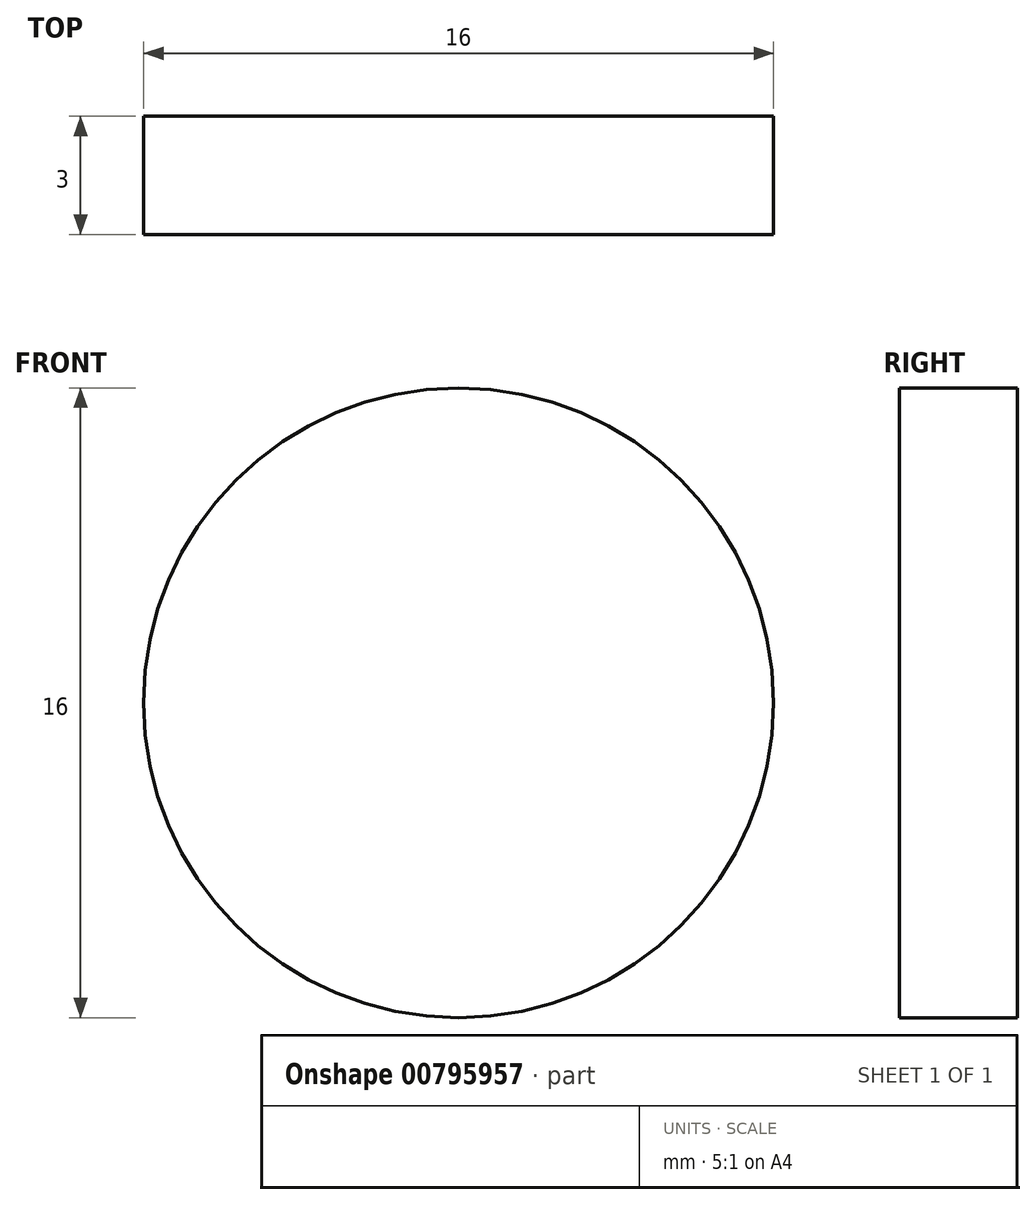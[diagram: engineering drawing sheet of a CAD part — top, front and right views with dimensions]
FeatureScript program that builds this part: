
annotation { "Feature Type Name" : "Feature", "Feature Type Description" : "" }
export const myFeature = defineFeature(function(context is Context, id is Id, definition is map)
    precondition{}
    {
        {
            var Q0;
            Q0=qCreatedBy(makeId("Front.planeOp"),FACE);
            var sketch = newSketch(context, id + "F0", { "sketchPlane" : qUnion([Q0])});
            skLineSegment(sketch, "E0.bottom", {"start": v(72.5, 15) * mm, "end": v(-72.5, 15) * mm});
            skLineSegment(sketch, "E0.top", {"start": v(72.5, -15) * mm, "end": v(-72.5, -15) * mm});
            skLineSegment(sketch, "E0.left", {"start": v(72.5, 15) * mm, "end": v(72.5, -15) * mm});
            skLineSegment(sketch, "E0.right", {"start": v(-72.5, 15) * mm, "end": v(-72.5, -15) * mm});
            skPoint(sketch, "E0.middle", {"position": v(0, 0) * mm});
            skSolve(sketch);
        }
        {
            var Q0;
            Q0=makeQuery(id+"F0.imprint","IMPRINT",FACE,{"disambiguationData":[TD([[makeQuery(id+"F0.imprint","IMPRINT",EDGE,{"derivedFrom":sQuery(id+"F0.wireOp",EDGE,"E0.bottom")}),1.0]])]});
            extrude(context, id + "F1", {"entities" : qUnion([Q0]), "depth" : 3 * mm, "offsetDistance" : 25 * mm});
        }
        {
            var Q0;
            Q0=makeQuery(id+"F1.opExtrude","CAP_FACE",FACE,{"disambiguationData":[OSD([sQuery(id+"F0.wireOp",EDGE,"E0.bottom"),sQuery(id+"F0.wireOp",EDGE,"E0.top"),sQuery(id+"F0.wireOp",EDGE,"E0.left"),sQuery(id+"F0.wireOp",EDGE,"E0.right")])],"isStart":false});
            var sketch = newSketch(context, id + "F2", { "sketchPlane" : qUnion([Q0])});
            skLineSegment(sketch, "E1", {"start": v(-75, -15) * mm, "end": v(-72.5, -15) * mm, "construction": true});
            skLineSegment(sketch, "E2.bottom", {"start": v(-75, -15) * mm, "end": v(-65, -15) * mm});
            skLineSegment(sketch, "E2.top", {"start": v(-75, -12) * mm, "end": v(-65, -12) * mm});
            skLineSegment(sketch, "E2.left", {"start": v(-75, -15) * mm, "end": v(-75, -12) * mm});
            skLineSegment(sketch, "E2.right", {"start": v(-65, -15) * mm, "end": v(-65, -12) * mm});
            skLineSegment(sketch, "E3.0.1.0", {"start": v(-75, 15) * mm, "end": v(-65, 15) * mm});
            skLineSegment(sketch, "E3.0.1.1", {"start": v(-75, 12) * mm, "end": v(-65, 12) * mm});
            skLineSegment(sketch, "E3.0.1.2", {"start": v(-65, 12) * mm, "end": v(-65, 15) * mm});
            skLineSegment(sketch, "E3.0.1.3", {"start": v(-75, 12) * mm, "end": v(-75, 15) * mm});
            skLineSegment(sketch, "E3.1.0.0", {"start": v(-55, -12) * mm, "end": v(-45, -12) * mm});
            skLineSegment(sketch, "E3.1.0.1", {"start": v(-55, -15) * mm, "end": v(-45, -15) * mm});
            skLineSegment(sketch, "E3.1.0.2", {"start": v(-45, -15) * mm, "end": v(-45, -12) * mm});
            skLineSegment(sketch, "E3.1.0.3", {"start": v(-55, -15) * mm, "end": v(-55, -12) * mm});
            skLineSegment(sketch, "E3.1.1.0", {"start": v(-55, 15) * mm, "end": v(-45, 15) * mm});
            skLineSegment(sketch, "E3.1.1.1", {"start": v(-55, 12) * mm, "end": v(-45, 12) * mm});
            skLineSegment(sketch, "E3.1.1.2", {"start": v(-45, 12) * mm, "end": v(-45, 15) * mm});
            skLineSegment(sketch, "E3.1.1.3", {"start": v(-55, 12) * mm, "end": v(-55, 15) * mm});
            skLineSegment(sketch, "E3.2.0.0", {"start": v(-35, -12) * mm, "end": v(-25, -12) * mm});
            skLineSegment(sketch, "E3.2.0.1", {"start": v(-35, -15) * mm, "end": v(-25, -15) * mm});
            skLineSegment(sketch, "E3.2.0.2", {"start": v(-25, -15) * mm, "end": v(-25, -12) * mm});
            skLineSegment(sketch, "E3.2.0.3", {"start": v(-35, -15) * mm, "end": v(-35, -12) * mm});
            skLineSegment(sketch, "E3.2.1.0", {"start": v(-35, 15) * mm, "end": v(-25, 15) * mm});
            skLineSegment(sketch, "E3.2.1.1", {"start": v(-35, 12) * mm, "end": v(-25, 12) * mm});
            skLineSegment(sketch, "E3.2.1.2", {"start": v(-25, 12) * mm, "end": v(-25, 15) * mm});
            skLineSegment(sketch, "E3.2.1.3", {"start": v(-35, 12) * mm, "end": v(-35, 15) * mm});
            skLineSegment(sketch, "E3.3.0.0", {"start": v(-15, -12) * mm, "end": v(-5, -12) * mm});
            skLineSegment(sketch, "E3.3.0.1", {"start": v(-15, -15) * mm, "end": v(-5, -15) * mm});
            skLineSegment(sketch, "E3.3.0.2", {"start": v(-5, -15) * mm, "end": v(-5, -12) * mm});
            skLineSegment(sketch, "E3.3.0.3", {"start": v(-15, -15) * mm, "end": v(-15, -12) * mm});
            skLineSegment(sketch, "E3.3.1.0", {"start": v(-15, 15) * mm, "end": v(-5, 15) * mm});
            skLineSegment(sketch, "E3.3.1.1", {"start": v(-15, 12) * mm, "end": v(-5, 12) * mm});
            skLineSegment(sketch, "E3.3.1.2", {"start": v(-5, 12) * mm, "end": v(-5, 15) * mm});
            skLineSegment(sketch, "E3.3.1.3", {"start": v(-15, 12) * mm, "end": v(-15, 15) * mm});
            skLineSegment(sketch, "E3.4.0.0", {"start": v(5, -12) * mm, "end": v(15, -12) * mm});
            skLineSegment(sketch, "E3.4.0.1", {"start": v(5, -15) * mm, "end": v(15, -15) * mm});
            skLineSegment(sketch, "E3.4.0.2", {"start": v(15, -15) * mm, "end": v(15, -12) * mm});
            skLineSegment(sketch, "E3.4.0.3", {"start": v(5, -15) * mm, "end": v(5, -12) * mm});
            skLineSegment(sketch, "E3.4.1.0", {"start": v(5, 15) * mm, "end": v(15, 15) * mm});
            skLineSegment(sketch, "E3.4.1.1", {"start": v(5, 12) * mm, "end": v(15, 12) * mm});
            skLineSegment(sketch, "E3.4.1.2", {"start": v(15, 12) * mm, "end": v(15, 15) * mm});
            skLineSegment(sketch, "E3.4.1.3", {"start": v(5, 12) * mm, "end": v(5, 15) * mm});
            skLineSegment(sketch, "E3.5.0.0", {"start": v(25, -12) * mm, "end": v(35, -12) * mm});
            skLineSegment(sketch, "E3.5.0.1", {"start": v(25, -15) * mm, "end": v(35, -15) * mm});
            skLineSegment(sketch, "E3.5.0.2", {"start": v(35, -15) * mm, "end": v(35, -12) * mm});
            skLineSegment(sketch, "E3.5.0.3", {"start": v(25, -15) * mm, "end": v(25, -12) * mm});
            skLineSegment(sketch, "E3.5.1.0", {"start": v(25, 15) * mm, "end": v(35, 15) * mm});
            skLineSegment(sketch, "E3.5.1.1", {"start": v(25, 12) * mm, "end": v(35, 12) * mm});
            skLineSegment(sketch, "E3.5.1.2", {"start": v(35, 12) * mm, "end": v(35, 15) * mm});
            skLineSegment(sketch, "E3.5.1.3", {"start": v(25, 12) * mm, "end": v(25, 15) * mm});
            skLineSegment(sketch, "E3.6.0.0", {"start": v(45, -12) * mm, "end": v(55, -12) * mm});
            skLineSegment(sketch, "E3.6.0.1", {"start": v(45, -15) * mm, "end": v(55, -15) * mm});
            skLineSegment(sketch, "E3.6.0.2", {"start": v(55, -15) * mm, "end": v(55, -12) * mm});
            skLineSegment(sketch, "E3.6.0.3", {"start": v(45, -15) * mm, "end": v(45, -12) * mm});
            skLineSegment(sketch, "E3.6.1.0", {"start": v(45, 15) * mm, "end": v(55, 15) * mm});
            skLineSegment(sketch, "E3.6.1.1", {"start": v(45, 12) * mm, "end": v(55, 12) * mm});
            skLineSegment(sketch, "E3.6.1.2", {"start": v(55, 12) * mm, "end": v(55, 15) * mm});
            skLineSegment(sketch, "E3.6.1.3", {"start": v(45, 12) * mm, "end": v(45, 15) * mm});
            skLineSegment(sketch, "E3.direction1", {"start": v(-75, -12) * mm, "end": v(-55, -12) * mm, "construction": true});
            skLineSegment(sketch, "E3.direction2", {"start": v(-75, -12) * mm, "end": v(-75, 15) * mm, "construction": true});
            skLineSegment(sketch, "E4.0.7.0", {"start": v(65, -12) * mm, "end": v(75, -12) * mm});
            skLineSegment(sketch, "E4.3.7.0", {"start": v(65, -15) * mm, "end": v(75, -15) * mm});
            skLineSegment(sketch, "E4.6.7.0", {"start": v(75, -15) * mm, "end": v(75, -12) * mm});
            skLineSegment(sketch, "E4.9.7.0", {"start": v(65, -15) * mm, "end": v(65, -12) * mm});
            skLineSegment(sketch, "E4.0.7.1", {"start": v(65, 15) * mm, "end": v(75, 15) * mm});
            skLineSegment(sketch, "E4.3.7.1", {"start": v(65, 12) * mm, "end": v(75, 12) * mm});
            skLineSegment(sketch, "E4.6.7.1", {"start": v(75, 12) * mm, "end": v(75, 15) * mm});
            skLineSegment(sketch, "E4.9.7.1", {"start": v(65, 12) * mm, "end": v(65, 15) * mm});
            skSolve(sketch);
        }
        {
            var Q0;
            Q0=qSketchRegion(id+"F2",true);
            extrude(context, id + "F3", {"entities" : qUnion([Q0]), "operationType" : NewBodyOperationType.REMOVE, "oppositeDirection" : true, "depth" : 25 * mm, "offsetDistance" : 25 * mm});
        }
        {
            var Q0;
            Q0=makeQuery(id+"F1.opExtrude","SWEPT_FACE",FACE,{"disambiguationData":[OSD([sQuery(id+"F0.wireOp",EDGE,"E0.left")])]});
            var Q1;
            Q1=makeQuery(id+"F1.opExtrude","SWEPT_FACE",FACE,{"disambiguationData":[OSD([sQuery(id+"F0.wireOp",EDGE,"E0.right")])]});
            extrude(context, id + "F4", {"entities" : qUnion([Q0, Q1]), "operationType" : NewBodyOperationType.ADD, "depth" : 5 * mm, "offsetDistance" : 25 * mm});
        }
        {
            var Q0;
            Q0=makeQuery(id+"F1.opExtrude","SWEPT_FACE",FACE,{"disambiguationData":[OSD([sQuery(id+"F0.wireOp",EDGE,"E0.right")])]});
            extrude(context, id + "F5", {"entities" : qUnion([Q0]), "operationType" : NewBodyOperationType.ADD, "depth" : 5 * mm, "offsetDistance" : 25 * mm});
        }
        {
            var Q0;
            {var subQ0=sQuery(id+"F0.wireOp",EDGE,"E0.right");var subQ1=sQuery(id+"F0.wireOp",EDGE,"E0.left");Q0=makeQuery(id+"F5.boolean.opBoolean","MERGE",FACE,{"derivedFrom":[makeQuery(id+"F4.boolean.opBoolean","MERGE",FACE,{"derivedFrom":[makeQuery(id+"F1.opExtrude","CAP_FACE",FACE,{"disambiguationData":[OSD([sQuery(id+"F0.wireOp",EDGE,"E0.bottom"),sQuery(id+"F0.wireOp",EDGE,"E0.top"),subQ1,subQ0])],"isStart":true}),makeQuery(id+"F4.opExtrude","SWEPT_FACE",FACE,{"disambiguationData":[OSD([subQ1]),TDD([makeQuery(id+"F1.opExtrude","CAP_EDGE",EDGE,{"disambiguationData":[OSD([subQ1])],"isStart":true})])]})]}),makeQuery(id+"F5.opExtrude","SWEPT_FACE",FACE,{"disambiguationData":[OSD([subQ0]),TDD([makeQuery(id+"F1.opExtrude","CAP_EDGE",EDGE,{"disambiguationData":[OSD([subQ0])],"isStart":true})])]})]});}
            var sketch = newSketch(context, id + "F6", { "sketchPlane" : qUnion([Q0])});
            skLineSegment(sketch, "E5.bottom", {"start": v(75.5, -12) * mm, "end": v(72.5, -12) * mm});
            skLineSegment(sketch, "E5.top", {"start": v(75.5, 0) * mm, "end": v(72.5, 0) * mm});
            skLineSegment(sketch, "E5.left", {"start": v(75.5, -12) * mm, "end": v(75.5, 0) * mm});
            skLineSegment(sketch, "E5.right", {"start": v(72.5, -12) * mm, "end": v(72.5, 0) * mm});
            skLineSegment(sketch, "E6", {"start": v(0, 15) * mm, "end": v(0, -24.82) * mm, "construction": true});
            skLineSegment(sketch, "E7.MirrorCS", {"start": v(-75.5, -12) * mm, "end": v(-75.5, 0) * mm});
            skLineSegment(sketch, "E8.MirrorCS", {"start": v(-75.5, 0) * mm, "end": v(-72.5, 0) * mm});
            skLineSegment(sketch, "E9.MirrorCS", {"start": v(-75.5, -12) * mm, "end": v(-72.5, -12) * mm});
            skLineSegment(sketch, "E10.MirrorCS", {"start": v(-72.5, -12) * mm, "end": v(-72.5, 0) * mm});
            skSolve(sketch);
        }
        {
            var Q0;
            Q0=makeQuery(id+"F6.imprint","IMPRINT",FACE,{"disambiguationData":[TD([[makeQuery(id+"F6.imprint","IMPRINT",EDGE,{"derivedFrom":sQuery(id+"F6.wireOp",EDGE,"E7.MirrorCS")}),-1.0]])]});
            var Q1;
            Q1=makeQuery(id+"F6.imprint","IMPRINT",FACE,{"disambiguationData":[TD([[makeQuery(id+"F6.imprint","IMPRINT",EDGE,{"derivedFrom":sQuery(id+"F6.wireOp",EDGE,"E5.bottom")}),-1.0]])]});
            extrude(context, id + "F7", {"entities" : qUnion([Q0, Q1]), "operationType" : NewBodyOperationType.REMOVE, "oppositeDirection" : true, "depth" : 25 * mm, "offsetDistance" : 25 * mm});
        }
        {
            var Q0;
            {var subQ0=sQuery(id+"F0.wireOp",EDGE,"E0.right");var subQ1=sQuery(id+"F0.wireOp",EDGE,"E0.left");Q0=makeQuery(id+"F5.boolean.opBoolean","MERGE",FACE,{"derivedFrom":[makeQuery(id+"F4.boolean.opBoolean","MERGE",FACE,{"derivedFrom":[makeQuery(id+"F1.opExtrude","CAP_FACE",FACE,{"disambiguationData":[OSD([sQuery(id+"F0.wireOp",EDGE,"E0.bottom"),sQuery(id+"F0.wireOp",EDGE,"E0.top"),subQ1,subQ0])],"isStart":false}),makeQuery(id+"F4.opExtrude","SWEPT_FACE",FACE,{"disambiguationData":[OSD([subQ1]),TDD([makeQuery(id+"F1.opExtrude","CAP_EDGE",EDGE,{"disambiguationData":[OSD([subQ1])],"isStart":false})])]})]}),makeQuery(id+"F5.opExtrude","SWEPT_FACE",FACE,{"disambiguationData":[OSD([subQ0]),TDD([makeQuery(id+"F1.opExtrude","CAP_EDGE",EDGE,{"disambiguationData":[OSD([subQ0])],"isStart":false})])]})]});}
            var sketch = newSketch(context, id + "F8", { "sketchPlane" : qUnion([Q0])});
            skLineSegment(sketch, "E11", {"start": v(0, 15) * mm, "end": v(0, -18.51) * mm, "construction": true});
            skCircle(sketch, "E12", {"center": v(12.8, 2) * mm, "radius": 8 * mm});
            skCircle(sketch, "E13.MirrorC", {"center": v(-12.8, 2) * mm, "radius": 8 * mm});
            skSolve(sketch);
        }
        {
            var Q0;
            Q0=makeQuery(id+"F8.imprint","IMPRINT",FACE,{"disambiguationData":[TD([[makeQuery(id+"F8.imprint","IMPRINT",EDGE,{"derivedFrom":sQuery(id+"F8.wireOp",EDGE,"E13.MirrorC")}),-1.0]])]});
            var Q1;
            Q1=makeQuery(id+"F8.imprint","IMPRINT",FACE,{"disambiguationData":[TD([[makeQuery(id+"F8.imprint","IMPRINT",EDGE,{"derivedFrom":sQuery(id+"F8.wireOp",EDGE,"E12")}),1.0]])]});
            extrude(context, id + "F9", {"entities" : qUnion([Q0, Q1]), "operationType" : NewBodyOperationType.REMOVE, "oppositeDirection" : true, "depth" : 25 * mm, "offsetDistance" : 25 * mm});
        }
    });
